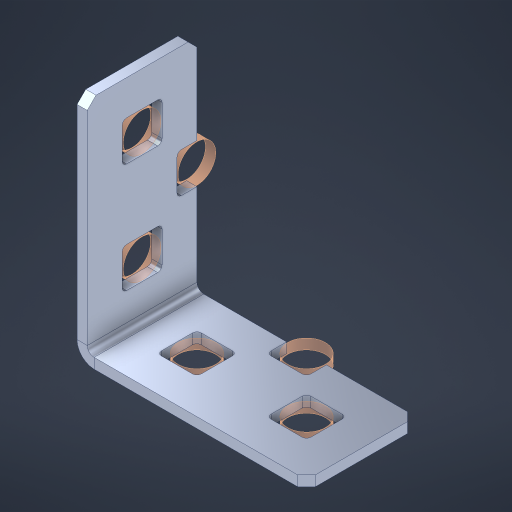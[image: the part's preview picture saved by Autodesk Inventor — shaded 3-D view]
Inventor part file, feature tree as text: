
AUTODESK INVENTOR PART (.ipt)
format: ipt  version: 2023 (Build 270158000, 158)  size: 452,608 bytes
history: native  units: in
note: dims shown in document units (in); Inventor stores cm internally (conversion verified against a paired STEP export)
features: other x78, extrude x70, sheet_metal_op x8, sketch x7, pattern_linear x2, mirror x1, chamfer x1
ambient origin geometry x8: Origin, YZ Plane, XZ Plane, XY Plane, X Axis, Y Axis, Z Axis, Center Point
bodies: Solid1 (feature_tree), Body (feature_tree)
feature tree (167):
  sheet_metal_op  "Flanges"
  sheet_metal_op  "Body Pattern"
  pattern_linear  "Center Pattern"  Spacing1=1.0in  [1 undecoded]
  other  "Arc Length"
  pattern_linear  "Notch Pattern"  Spacing1=0.1875in  [1 undecoded]
  other  "Diagonal Plane"
  mirror  "Everything Mirrored"
  chamfer  "End Chamfer"
  sketch  "Sketch1"  dims[d0=1.0in]
  other  "Plate1"
  sketch  "Sketch2"  dims[d1=0.5in]
  other  "Plate2"
  sheet_metal_op  "Bend1"
  sheet_metal_op  "Corner1"
  sketch  "Sketch8"  dims[d2=0.0469in]
  sketch  "Sketch9"  dims[d3=0.0469in]
  other  "Srf91"
  sheet_metal_op  "Body Pattern Sketch"
  other  "Srf92"
  sketch  "Sketch13"  dims[d4=0.0234in]
  sketch  "Sketch15"  dims[d5=0.0938in]
  sketch  "Sketch16"  dims[d6=0.0469in d7=1.0in d8=90.0deg d9=0.0312in d10=0.1875in d11=0.0469in d12=0.0469in d49=0.182in d50=0.02in d52=0.25in d53=0.0469in d54=0.0in d55=0.172in d56=1.0in d57=0.0in d60=0.3937in d62=0.5in d63=0.7874in d65=0.5in d85=0.1473in d86=0.1659in d89=0.0469in d90=0.0in d91=0.04in d92=0.0491in d95=2.5in d96=0.04in d97=0.25in d98=45.0deg d99=0.25in d106=0.182in d107=0.02in d108=0.5in d110=0.0469in d111=0.0in d112=0.172in d113=0.5in d114=0.0in d117=0.5in d123=0.25in d125=0.25in d126=0.0491in d127=0.1227in d128=0.08in d129=0.04in d130=2.5in]
  other  "Srf786"
  other  "Srf889"
  other  "Srf890"
  other  "Srf891"
  other  "Srf1275"
  other  "Srf1276"
  other  "Srf1277"
  other  "Srf1285"
  other  "Srf1286"
  other  "Srf1287"
  other  "Srf1445"
  other  "Srf1446"
  other  "Srf1447"
  other  "Srf1448"
  other  "Srf1449"
  other  "Srf1450"
  other  "Srf1451"
  other  "Srf1452"
  other  "Srf1453"
  other  "Srf1454"
  other  "Srf1455"
  other  "Srf1456"
  other  "Srf1457"
  other  "Srf1458"
  other  "Srf1459"
  other  "Srf1460"
  other  "Srf1461"
  other  "Srf1462"
  other  "Srf1463"
  other  "Srf1464"
  other  "Srf1465"
  other  "Srf1466"
  other  "Srf1467"
  other  "Srf1468"
  other  "Srf1469"
  other  "Srf1470"
  other  "Srf1471"
  other  "Srf1472"
  other  "Srf1473"
  other  "Srf1474"
  other  "Srf1537"
  other  "Srf1538"
  other  "Srf1539"
  other  "Srf1540"
  other  "Srf1541"
  other  "Srf1542"
  other  "Srf1543"
  other  "Srf1544"
  other  "Srf1545"
  other  "Srf1546"
  other  "Srf1547"
  other  "Srf1548"
  other  "Srf1549"
  other  "Srf1550"
  other  "Srf1551"
  other  "Srf1552"
  other  "Srf1553"
  other  "Srf1554"
  other  "Srf1555"
  other  "Srf1556"
  other  "Srf1557"
  other  "Srf1558"
  other  "Srf1559"
  other  "Srf1560"
  other  "Srf1561"
  other  "Srf1562"
  other  "Srf1563"
  other  "Srf1564"
  other  "Srf1565"
  other  "Srf1566"
  sheet_metal_op  "Body Stamp"
  sheet_metal_op  "Body Circle"
  other  "Center Stamp"
  other  "Center Circle"
  sheet_metal_op  "Notch"
  extrude  "ExtrusionSrf92"  Depth=0.0469in
  extrude  "ExtrusionSrf889"  Depth=0.0469in
  extrude  "ExtrusionSrf890"  Depth=0.182in
  extrude  "ExtrusionSrf891"  Depth=0.02in
  extrude  "ExtrusionSrf1275"  Depth=0.25in
  extrude  "ExtrusionSrf1276"  Depth=0.0469in
  extrude  "ExtrusionSrf1345"  TaperAngle=0.0deg  [1 undecoded]
  extrude  "ExtrusionSrf1346"  Depth=0.25in
  extrude  "ExtrusionSrf1347"  Depth=1.0in TaperAngle=0.0deg
  extrude  "ExtrusionSrf1348"  Depth=0.3937in
  extrude  "ExtrusionSrf1445"  Depth=0.5in
  extrude  "ExtrusionSrf1446"  Depth=0.25in
  extrude  "ExtrusionSrf1447"  Depth=0.25in
  extrude  "ExtrusionSrf1448"  Depth=0.0469in
  extrude  "ExtrusionSrf1449"  Depth=0.25in TaperAngle=0.0deg
  extrude  "ExtrusionSrf1450"  Depth=0.25in
  extrude  "ExtrusionSrf1451"  Depth=0.25in TaperAngle=45.0deg
  extrude  "ExtrusionSrf1452"  Depth=0.25in
  extrude  "ExtrusionSrf1453"  Depth=0.182in
  extrude  "ExtrusionSrf1454"  Depth=0.02in
  extrude  "ExtrusionSrf1455"  Depth=0.5in
  extrude  "ExtrusionSrf1456"  Depth=0.0469in
  extrude  "ExtrusionSrf1457"  TaperAngle=0.0deg  [1 undecoded]
  extrude  "ExtrusionSrf1458"  Depth=0.25in
  extrude  "ExtrusionSrf1459"  Depth=0.5in TaperAngle=0.0deg
  extrude  "ExtrusionSrf1460"  Depth=0.5in
  extrude  "ExtrusionSrf1461"  Depth=0.25in
  extrude  "ExtrusionSrf1462"  Depth=0.25in
  extrude  "ExtrusionSrf1463"  Depth=0.25in
  extrude  "ExtrusionSrf1464"  Depth=0.25in
  extrude  "ExtrusionSrf1465"  Depth=0.25in
  extrude  "ExtrusionSrf1466"  Depth=0.25in
  extrude  "ExtrusionSrf1467"  Depth=0.25in
  extrude  "ExtrusionSrf1468"  [1 undecoded]
  extrude  "ExtrusionSrf1469"  [1 undecoded]
  extrude  "ExtrusionSrf1470"  [1 undecoded]
  extrude  "ExtrusionSrf1471"  [1 undecoded]
  extrude  "ExtrusionSrf1472"  [1 undecoded]
  extrude  "ExtrusionSrf1473"  [1 undecoded]
  extrude  "ExtrusionSrf1474"  [1 undecoded]
  extrude  "ExtrusionSrf1537"  [1 undecoded]
  extrude  "ExtrusionSrf1538"  [1 undecoded]
  extrude  "ExtrusionSrf1539"  [1 undecoded]
  extrude  "ExtrusionSrf1540"  [1 undecoded]
  extrude  "ExtrusionSrf1541"  [1 undecoded]
  extrude  "ExtrusionSrf1542"  [1 undecoded]
  extrude  "ExtrusionSrf1543"  [1 undecoded]
  extrude  "ExtrusionSrf1544"  [1 undecoded]
  extrude  "ExtrusionSrf1545"  [1 undecoded]
  extrude  "ExtrusionSrf1546"  [1 undecoded]
  extrude  "ExtrusionSrf1547"  [1 undecoded]
  extrude  "ExtrusionSrf1548"  [1 undecoded]
  extrude  "ExtrusionSrf1549"  [1 undecoded]
  extrude  "ExtrusionSrf1550"  [1 undecoded]
  extrude  "ExtrusionSrf1551"  [1 undecoded]
  extrude  "ExtrusionSrf1552"  [1 undecoded]
  extrude  "ExtrusionSrf1553"  [1 undecoded]
  extrude  "ExtrusionSrf1554"  [1 undecoded]
  extrude  "ExtrusionSrf1555"  [1 undecoded]
  extrude  "ExtrusionSrf1556"  [1 undecoded]
  extrude  "ExtrusionSrf1557"  [1 undecoded]
  extrude  "ExtrusionSrf1558"  [1 undecoded]
  extrude  "ExtrusionSrf1559"  [1 undecoded]
  extrude  "ExtrusionSrf1560"  [1 undecoded]
  extrude  "ExtrusionSrf1561"  [1 undecoded]
  extrude  "ExtrusionSrf1562"  [1 undecoded]
  extrude  "ExtrusionSrf1563"  [1 undecoded]
  extrude  "ExtrusionSrf1564"  [1 undecoded]
  extrude  "ExtrusionSrf1565"  [1 undecoded]
  extrude  "ExtrusionSrf1566"  [1 undecoded]
note: 41 required parameter values undecoded (feature->parameter linkage not recoverable at this tier; creation-order binding heuristic only, values carry confidence <= 0.55)
